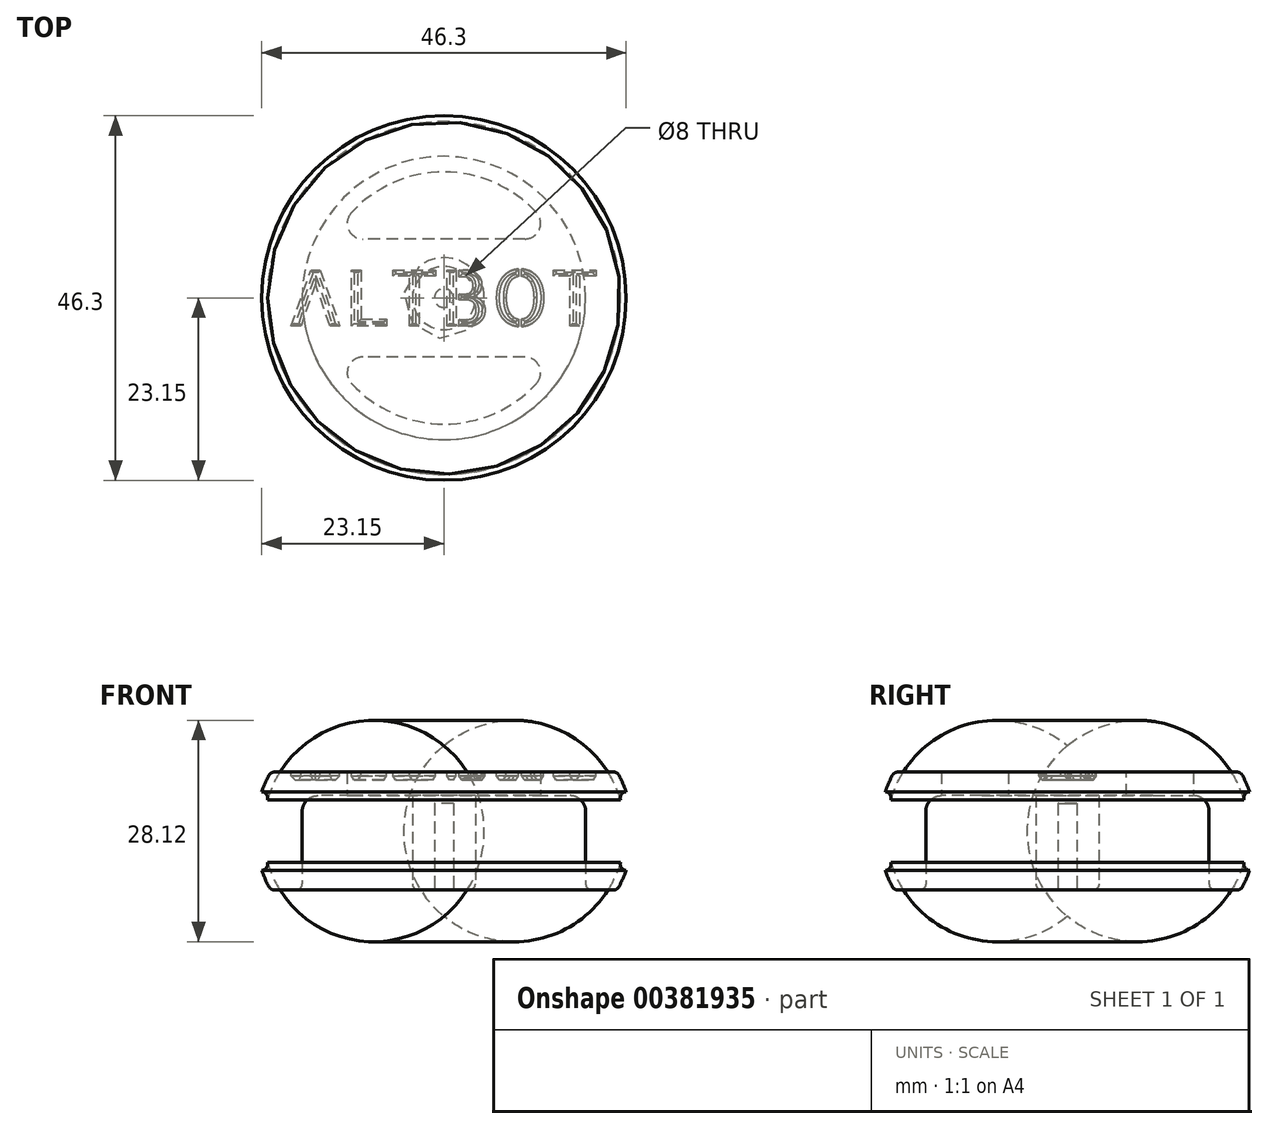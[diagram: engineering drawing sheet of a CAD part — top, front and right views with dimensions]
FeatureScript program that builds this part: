
annotation { "Feature Type Name" : "Feature", "Feature Type Description" : "" }
export const myFeature = defineFeature(function(context is Context, id is Id, definition is map)
    precondition{}
    {
        {
            assignVariable(context, id + "F0", {"name" : "EixoAltura", "anyValue" : 12});
        }
        {
            var Q0;
            Q0=qCreatedBy(makeId("Top.planeOp"),FACE);
            var sketch = newSketch(context, id + "F1", { "sketchPlane" : qUnion([Q0])});
            skCircle(sketch, "E0", {"center": v(0, 0) * mm, "radius": 4 * mm});
            skCircle(sketch, "E1", {"center": v(0, 0) * mm, "radius": 1.2 * mm});
            skSolve(sketch);
        }
        {
            var Q0;
            Q0=makeQuery(id+"F1.imprint","IMPRINT",FACE,{"disambiguationData":[TD([[makeQuery(id+"F1.imprint","IMPRINT",EDGE,{"derivedFrom":sQuery(id+"F1.wireOp",EDGE,"E1")}),1.0]])]});
            var Q1;
            Q1=makeQuery(id+"F1.imprint","IMPRINT",FACE,{"disambiguationData":[TD([[makeQuery(id+"F1.imprint","IMPRINT",EDGE,{"derivedFrom":sQuery(id+"F1.wireOp",EDGE,"E0")}),1.0]])]});
            extrude(context, id + "F2", {"entities" : qUnion([Q0, Q1]), "depth" : (getVariable(context, 'EixoAltura')) * mm});
        }
        {
            var Q0;
            Q0=makeQuery(id+"F1.imprint","IMPRINT",FACE,{"disambiguationData":[TD([[makeQuery(id+"F1.imprint","IMPRINT",EDGE,{"derivedFrom":sQuery(id+"F1.wireOp",EDGE,"E1")}),1.0]])]});
            var Q1;
            Q1 = qSketchRegion(id + "F4", true);
            extrude(context, id + "F3", {"entities" : qUnion([Q0, Q1]), "operationType" : NewBodyOperationType.REMOVE, "depth" : (getVariable(context, 'EixoAltura') - 1) * mm});
        }
        {
            var Q0;
            Q0=qCreatedBy(makeId("Right.planeOp"),FACE);
            var sketch = newSketch(context, id + "F4", { "sketchPlane" : qUnion([Q0])});
            skLineSegment(sketch, "E2", {"start": v(0, -22.32) * mm, "end": v(0, 36.65) * mm, "construction": true});
            skLineSegment(sketch, "E3", {"start": v(4, 12) * mm, "end": v(4, 0) * mm});
            skLineSegment(sketch, "E4", {"start": v(-4, 0) * mm, "end": v(-4, 12) * mm});
            skLineSegment(sketch, "E5", {"start": v(4, 12) * mm, "end": v(18, 12) * mm});
            skLineSegment(sketch, "E6", {"start": v(18, 12) * mm, "end": v(18, 0) * mm});
            skLineSegment(sketch, "E7", {"start": v(18, 0) * mm, "end": v(22, 0) * mm});
            skLineSegment(sketch, "E8", {"start": v(22, 0) * mm, "end": v(22, 15) * mm, "construction": true});
            skLineSegment(sketch, "E9", {"start": v(22, 15) * mm, "end": v(-22, 15) * mm});
            skLineSegment(sketch, "E10", {"start": v(-22, 15) * mm, "end": v(-22, 0) * mm, "construction": true});
            skLineSegment(sketch, "E11", {"start": v(-22, 0) * mm, "end": v(-18, 0) * mm});
            skLineSegment(sketch, "E12", {"start": v(-18, 0) * mm, "end": v(-18, 12) * mm});
            skLineSegment(sketch, "E13", {"start": v(-18, 12) * mm, "end": v(-4, 12) * mm});
            skLineSegment(sketch, "E14", {"start": v(22, 7.5) * mm, "end": v(24, 7.5) * mm, "construction": true});
            skPoint(sketch, "E14.endSnap0", {"position": v(22, 7.5) * mm});
            skLineSegment(sketch, "E15", {"start": v(-22, 7.5) * mm, "end": v(-24, 7.5) * mm, "construction": true});
            skPoint(sketch, "E15.endSnap0", {"position": v(-22, 7.5) * mm});
            skArc(sketch, "E16", {"start": v(22, 0) * mm, "mid": v(22.63, 1.22) * mm, "end": v(23.15, 2.5) * mm});
            skArc(sketch, "E17", {"start": v(-22, 15) * mm, "mid": v(-22.63, 13.78) * mm, "end": v(-23.15, 12.5) * mm});
            skArc(sketch, "E18.0", {"start": v(19.9, -1.3) * mm, "mid": v(21.14, 0.51) * mm, "end": v(22.08, 2.5) * mm, "construction": true});
            skArc(sketch, "E19.0", {"start": v(-19.83, 17.16) * mm, "mid": v(-21.44, 14.96) * mm, "end": v(-22.61, 12.5) * mm, "construction": true});
            skLineSegment(sketch, "E20.bottom", {"start": v(-19.5, 12.5) * mm, "end": v(-22.61, 12.5) * mm, "construction": true});
            skLineSegment(sketch, "E20.top", {"start": v(-19.5, 2.5) * mm, "end": v(-22.61, 2.5) * mm, "construction": true});
            skLineSegment(sketch, "E20.left", {"start": v(-19.5, 12.5) * mm, "end": v(-19.5, 2.5) * mm, "construction": true});
            skLineSegment(sketch, "E20.right", {"start": v(-24.5, 12.5) * mm, "end": v(-24.5, 2.5) * mm, "construction": true});
            skLineSegment(sketch, "E21.bottom", {"start": v(19.5, 12.5) * mm, "end": v(22.08, 12.5) * mm, "construction": true});
            skLineSegment(sketch, "E21.top", {"start": v(19.5, 2.5) * mm, "end": v(22.08, 2.5) * mm, "construction": true});
            skLineSegment(sketch, "E21.left", {"start": v(19.5, 12.5) * mm, "end": v(19.5, 2.5) * mm, "construction": true});
            skLineSegment(sketch, "E21.right", {"start": v(24.5, 12.5) * mm, "end": v(24.5, 2.5) * mm, "construction": true});
            skArc(sketch, "E22", {"start": v(-23.15, 12.5) * mm, "mid": v(-24, 7.5) * mm, "end": v(-23.15, 2.5) * mm, "construction": true});
            skLineSegment(sketch, "E23", {"start": v(-22.61, 12.5) * mm, "end": v(-23.15, 12.5) * mm});
            skArc(sketch, "E24", {"start": v(-22.61, 12.5) * mm, "mid": v(-23.5, 7.5) * mm, "end": v(-22.61, 2.5) * mm});
            skLineSegment(sketch, "E25", {"start": v(-23.15, 12.5) * mm, "end": v(-24.5, 12.5) * mm, "construction": true});
            skArc(sketch, "E26", {"start": v(-23.15, 2.5) * mm, "mid": v(-22.63, 1.22) * mm, "end": v(-22, 0) * mm});
            skLineSegment(sketch, "E27", {"start": v(-23.15, 2.5) * mm, "end": v(-24.5, 2.5) * mm, "construction": true});
            skLineSegment(sketch, "E28", {"start": v(-22.61, 2.5) * mm, "end": v(-23.15, 2.5) * mm});
            skLineSegment(sketch, "E29", {"start": v(-22.61, 2.5) * mm, "end": v(-22.61, 2.5) * mm});
            skLineSegment(sketch, "E30", {"start": v(23.15, 12.5) * mm, "end": v(24.5, 12.5) * mm, "construction": true});
            skArc(sketch, "E31", {"start": v(23.15, 12.5) * mm, "mid": v(22.63, 13.78) * mm, "end": v(22, 15) * mm});
            skArc(sketch, "E32", {"start": v(22.08, 12.5) * mm, "mid": v(21.14, 14.49) * mm, "end": v(19.9, 16.3) * mm, "construction": true});
            skLineSegment(sketch, "E33", {"start": v(22.08, 12.5) * mm, "end": v(23.15, 12.5) * mm});
            skArc(sketch, "E34", {"start": v(23.15, 2.5) * mm, "mid": v(24, 7.5) * mm, "end": v(23.15, 12.5) * mm, "construction": true});
            skLineSegment(sketch, "E35", {"start": v(23.15, 2.5) * mm, "end": v(24.5, 2.5) * mm, "construction": true});
            skArc(sketch, "E36", {"start": v(22.08, 2.5) * mm, "mid": v(23, 7.5) * mm, "end": v(22.08, 12.5) * mm});
            skLineSegment(sketch, "E37", {"start": v(22.08, 2.5) * mm, "end": v(23.15, 2.5) * mm});
            skArc(sketch, "E38", {"start": v(-22.61, 2.5) * mm, "mid": v(-21.44, 0.04) * mm, "end": v(-19.83, -2.16) * mm, "construction": true});
            skLineSegment(sketch, "E39", {"start": v(4, 12) * mm, "end": v(4, 12) * mm});
            skLineSegment(sketch, "E40", {"start": v(4, 12) * mm, "end": v(-4, 12) * mm});
            skLineSegment(sketch, "E41", {"start": v(0, 12) * mm, "end": v(0, 15) * mm});
            skSolve(sketch);
        }
        {
            var Q0;
            Q0=makeQuery(id+"F4.imprint","IMPRINT",FACE,{"disambiguationData":[TD([[makeQuery(id+"F4.imprint","IMPRINT",EDGE,{"derivedFrom":sQuery(id+"F4.wireOp",EDGE,"E5")}),1.0]])]});
            var Q1;
            Q1=sQuery(id+"F4.wireOp",EDGE,"E2");
            revolve(context, id + "F5", {"operationType" : NewBodyOperationType.ADD, "entities" : qUnion([Q0]), "axis" : qUnion([Q1]), "revolveType" : RevolveType.FULL});
        }
        {
            var Q0;
            Q0=makeQuery(id+"F5.opRevolve","SWEPT_FACE",FACE,{"disambiguationData":[OSD([sQuery(id+"F4.wireOp",EDGE,"E9")])]});
            var sketch = newSketch(context, id + "F6", { "sketchPlane" : qUnion([Q0])});
            skText(sketch, "E42", { "text": "ALTBOT", "fontName": "AllertaStencil-Regular.ttf"});
            const initialGuessF6  = {"E42": [-0.02, -0.00357, 1, 0, 0.00715]};
            skSetInitialGuess(sketch, initialGuessF6);
            skSolve(sketch);
        }
        {
            var Q0;
            Q0=makeQuery(id+"F6.imprint","IMPRINT",FACE,{"disambiguationData":[TD([[makeQuery(id+"F6.imprint","IMPRINT",EDGE,{"derivedFrom":sQuery(id+"F6.wireOp",EDGE,"E42.sketch_text.stroke-0")}),-1.0]])]});
            var Q1;
            Q1=makeQuery(id+"F6.imprint","IMPRINT",FACE,{"disambiguationData":[TD([[makeQuery(id+"F6.imprint","IMPRINT",EDGE,{"derivedFrom":sQuery(id+"F6.wireOp",EDGE,"E42.sketch_text.stroke-11")}),-1.0]])]});
            var Q2;
            Q2=makeQuery(id+"F6.imprint","IMPRINT",FACE,{"disambiguationData":[TD([[makeQuery(id+"F6.imprint","IMPRINT",EDGE,{"derivedFrom":sQuery(id+"F6.wireOp",EDGE,"E42.sketch_text.stroke-17")}),-1.0]])]});
            var Q3;
            Q3=makeQuery(id+"F6.imprint","IMPRINT",FACE,{"disambiguationData":[TD([[makeQuery(id+"F6.imprint","IMPRINT",EDGE,{"derivedFrom":sQuery(id+"F6.wireOp",EDGE,"E42.sketch_text.stroke-25")}),-1.0]])]});
            var Q4;
            Q4=makeQuery(id+"F6.imprint","IMPRINT",FACE,{"disambiguationData":[TD([[makeQuery(id+"F6.imprint","IMPRINT",EDGE,{"derivedFrom":sQuery(id+"F6.wireOp",EDGE,"E42.sketch_text.stroke-64")}),-1.0]])]});
            var Q5;
            Q5=makeQuery(id+"F6.imprint","IMPRINT",FACE,{"disambiguationData":[TD([[makeQuery(id+"F6.imprint","IMPRINT",EDGE,{"derivedFrom":sQuery(id+"F6.wireOp",EDGE,"E42.sketch_text.stroke-68")}),-1.0]])]});
            var Q6;
            Q6=makeQuery(id+"F6.imprint","IMPRINT",FACE,{"disambiguationData":[TD([[makeQuery(id+"F6.imprint","IMPRINT",EDGE,{"derivedFrom":sQuery(id+"F6.wireOp",EDGE,"E42.sketch_text.stroke-86")}),-1.0]])]});
            var Q7;
            Q7=makeQuery(id+"F6.imprint","IMPRINT",FACE,{"disambiguationData":[TD([[makeQuery(id+"F6.imprint","IMPRINT",EDGE,{"derivedFrom":sQuery(id+"F6.wireOp",EDGE,"E42.sketch_text.stroke-104")}),-1.0]])]});
            extrude(context, id + "F7", {"entities" : qUnion([Q0, Q1, Q2, Q3, Q4, Q5, Q6, Q7]), "operationType" : NewBodyOperationType.REMOVE, "oppositeDirection" : true, "depth" : .5 * mm});
        }
        {
            var Q0;
            Q0=makeQuery(id+"F7.boolean.opBoolean","COPY",FACE,{"derivedFrom":makeQuery(id+"F7.opExtrude","CAP_FACE",FACE,{"disambiguationData":[OSD([sQuery(id+"F6.wireOp",EDGE,"E42.sketch_text.stroke-0"),sQuery(id+"F6.wireOp",EDGE,"E42.sketch_text.stroke-1"),sQuery(id+"F6.wireOp",EDGE,"E42.sketch_text.stroke-2"),sQuery(id+"F6.wireOp",EDGE,"E42.sketch_text.stroke-3"),sQuery(id+"F6.wireOp",EDGE,"E42.sketch_text.stroke-4"),sQuery(id+"F6.wireOp",EDGE,"E42.sketch_text.stroke-5"),sQuery(id+"F6.wireOp",EDGE,"E42.sketch_text.stroke-6")])],"isStart":false})});
            var Q1;
            Q1=makeQuery(id+"F7.boolean.opBoolean","COPY",FACE,{"derivedFrom":makeQuery(id+"F7.opExtrude","CAP_FACE",FACE,{"disambiguationData":[OSD([sQuery(id+"F6.wireOp",EDGE,"E42.sketch_text.stroke-7"),sQuery(id+"F6.wireOp",EDGE,"E42.sketch_text.stroke-8"),sQuery(id+"F6.wireOp",EDGE,"E42.sketch_text.stroke-9"),sQuery(id+"F6.wireOp",EDGE,"E42.sketch_text.stroke-10")])],"isStart":false})});
            var Q2;
            Q2=makeQuery(id+"F7.boolean.opBoolean","COPY",FACE,{"derivedFrom":makeQuery(id+"F7.opExtrude","CAP_FACE",FACE,{"disambiguationData":[OSD([sQuery(id+"F6.wireOp",EDGE,"E42.sketch_text.stroke-11"),sQuery(id+"F6.wireOp",EDGE,"E42.sketch_text.stroke-12"),sQuery(id+"F6.wireOp",EDGE,"E42.sketch_text.stroke-13"),sQuery(id+"F6.wireOp",EDGE,"E42.sketch_text.stroke-14"),sQuery(id+"F6.wireOp",EDGE,"E42.sketch_text.stroke-15"),sQuery(id+"F6.wireOp",EDGE,"E42.sketch_text.stroke-16")])],"isStart":false})});
            var Q3;
            Q3=makeQuery(id+"F7.boolean.opBoolean","COPY",FACE,{"derivedFrom":makeQuery(id+"F7.opExtrude","CAP_FACE",FACE,{"disambiguationData":[OSD([sQuery(id+"F6.wireOp",EDGE,"E42.sketch_text.stroke-17"),sQuery(id+"F6.wireOp",EDGE,"E42.sketch_text.stroke-18"),sQuery(id+"F6.wireOp",EDGE,"E42.sketch_text.stroke-19"),sQuery(id+"F6.wireOp",EDGE,"E42.sketch_text.stroke-20"),sQuery(id+"F6.wireOp",EDGE,"E42.sketch_text.stroke-21"),sQuery(id+"F6.wireOp",EDGE,"E42.sketch_text.stroke-22"),sQuery(id+"F6.wireOp",EDGE,"E42.sketch_text.stroke-23"),sQuery(id+"F6.wireOp",EDGE,"E42.sketch_text.stroke-24")])],"isStart":false})});
            var Q4;
            Q4=makeQuery(id+"F7.boolean.opBoolean","COPY",FACE,{"derivedFrom":makeQuery(id+"F7.opExtrude","CAP_FACE",FACE,{"disambiguationData":[OSD([sQuery(id+"F6.wireOp",EDGE,"E42.sketch_text.stroke-64"),sQuery(id+"F6.wireOp",EDGE,"E42.sketch_text.stroke-65"),sQuery(id+"F6.wireOp",EDGE,"E42.sketch_text.stroke-66"),sQuery(id+"F6.wireOp",EDGE,"E42.sketch_text.stroke-67")])],"isStart":false})});
            var Q5;
            Q5=makeQuery(id+"F7.boolean.opBoolean","COPY",FACE,{"derivedFrom":makeQuery(id+"F7.opExtrude","CAP_FACE",FACE,{"disambiguationData":[OSD([sQuery(id+"F6.wireOp",EDGE,"E42.sketch_text.stroke-25"),sQuery(id+"F6.wireOp",EDGE,"E42.sketch_text.stroke-26"),sQuery(id+"F6.wireOp",EDGE,"E42.sketch_text.stroke-27"),sQuery(id+"F6.wireOp",EDGE,"E42.sketch_text.stroke-28"),sQuery(id+"F6.wireOp",EDGE,"E42.sketch_text.stroke-29"),sQuery(id+"F6.wireOp",EDGE,"E42.sketch_text.stroke-30"),sQuery(id+"F6.wireOp",EDGE,"E42.sketch_text.stroke-31"),sQuery(id+"F6.wireOp",EDGE,"E42.sketch_text.stroke-32"),sQuery(id+"F6.wireOp",EDGE,"E42.sketch_text.stroke-33"),sQuery(id+"F6.wireOp",EDGE,"E42.sketch_text.stroke-34"),sQuery(id+"F6.wireOp",EDGE,"E42.sketch_text.stroke-35"),sQuery(id+"F6.wireOp",EDGE,"E42.sketch_text.stroke-36"),sQuery(id+"F6.wireOp",EDGE,"E42.sketch_text.stroke-37"),sQuery(id+"F6.wireOp",EDGE,"E42.sketch_text.stroke-38"),sQuery(id+"F6.wireOp",EDGE,"E42.sketch_text.stroke-39"),sQuery(id+"F6.wireOp",EDGE,"E42.sketch_text.stroke-40"),sQuery(id+"F6.wireOp",EDGE,"E42.sketch_text.stroke-41"),sQuery(id+"F6.wireOp",EDGE,"E42.sketch_text.stroke-42"),sQuery(id+"F6.wireOp",EDGE,"E42.sketch_text.stroke-43"),sQuery(id+"F6.wireOp",EDGE,"E42.sketch_text.stroke-44"),sQuery(id+"F6.wireOp",EDGE,"E42.sketch_text.stroke-45"),sQuery(id+"F6.wireOp",EDGE,"E42.sketch_text.stroke-46"),sQuery(id+"F6.wireOp",EDGE,"E42.sketch_text.stroke-47"),sQuery(id+"F6.wireOp",EDGE,"E42.sketch_text.stroke-48"),sQuery(id+"F6.wireOp",EDGE,"E42.sketch_text.stroke-49"),sQuery(id+"F6.wireOp",EDGE,"E42.sketch_text.stroke-50"),sQuery(id+"F6.wireOp",EDGE,"E42.sketch_text.stroke-51"),sQuery(id+"F6.wireOp",EDGE,"E42.sketch_text.stroke-52"),sQuery(id+"F6.wireOp",EDGE,"E42.sketch_text.stroke-53"),sQuery(id+"F6.wireOp",EDGE,"E42.sketch_text.stroke-54"),sQuery(id+"F6.wireOp",EDGE,"E42.sketch_text.stroke-55"),sQuery(id+"F6.wireOp",EDGE,"E42.sketch_text.stroke-56"),sQuery(id+"F6.wireOp",EDGE,"E42.sketch_text.stroke-57"),sQuery(id+"F6.wireOp",EDGE,"E42.sketch_text.stroke-58"),sQuery(id+"F6.wireOp",EDGE,"E42.sketch_text.stroke-59"),sQuery(id+"F6.wireOp",EDGE,"E42.sketch_text.stroke-60"),sQuery(id+"F6.wireOp",EDGE,"E42.sketch_text.stroke-61"),sQuery(id+"F6.wireOp",EDGE,"E42.sketch_text.stroke-62"),sQuery(id+"F6.wireOp",EDGE,"E42.sketch_text.stroke-63")])],"isStart":false})});
            var Q6;
            Q6=makeQuery(id+"F7.boolean.opBoolean","COPY",FACE,{"derivedFrom":makeQuery(id+"F7.opExtrude","CAP_FACE",FACE,{"disambiguationData":[OSD([sQuery(id+"F6.wireOp",EDGE,"E42.sketch_text.stroke-68"),sQuery(id+"F6.wireOp",EDGE,"E42.sketch_text.stroke-69"),sQuery(id+"F6.wireOp",EDGE,"E42.sketch_text.stroke-70"),sQuery(id+"F6.wireOp",EDGE,"E42.sketch_text.stroke-71"),sQuery(id+"F6.wireOp",EDGE,"E42.sketch_text.stroke-72"),sQuery(id+"F6.wireOp",EDGE,"E42.sketch_text.stroke-73"),sQuery(id+"F6.wireOp",EDGE,"E42.sketch_text.stroke-74"),sQuery(id+"F6.wireOp",EDGE,"E42.sketch_text.stroke-75"),sQuery(id+"F6.wireOp",EDGE,"E42.sketch_text.stroke-76"),sQuery(id+"F6.wireOp",EDGE,"E42.sketch_text.stroke-77"),sQuery(id+"F6.wireOp",EDGE,"E42.sketch_text.stroke-78"),sQuery(id+"F6.wireOp",EDGE,"E42.sketch_text.stroke-79"),sQuery(id+"F6.wireOp",EDGE,"E42.sketch_text.stroke-80"),sQuery(id+"F6.wireOp",EDGE,"E42.sketch_text.stroke-81"),sQuery(id+"F6.wireOp",EDGE,"E42.sketch_text.stroke-82"),sQuery(id+"F6.wireOp",EDGE,"E42.sketch_text.stroke-83"),sQuery(id+"F6.wireOp",EDGE,"E42.sketch_text.stroke-84"),sQuery(id+"F6.wireOp",EDGE,"E42.sketch_text.stroke-85")])],"isStart":false})});
            var Q7;
            Q7=makeQuery(id+"F7.boolean.opBoolean","COPY",FACE,{"derivedFrom":makeQuery(id+"F7.opExtrude","CAP_FACE",FACE,{"disambiguationData":[OSD([sQuery(id+"F6.wireOp",EDGE,"E42.sketch_text.stroke-86"),sQuery(id+"F6.wireOp",EDGE,"E42.sketch_text.stroke-87"),sQuery(id+"F6.wireOp",EDGE,"E42.sketch_text.stroke-88"),sQuery(id+"F6.wireOp",EDGE,"E42.sketch_text.stroke-89"),sQuery(id+"F6.wireOp",EDGE,"E42.sketch_text.stroke-90"),sQuery(id+"F6.wireOp",EDGE,"E42.sketch_text.stroke-91"),sQuery(id+"F6.wireOp",EDGE,"E42.sketch_text.stroke-92"),sQuery(id+"F6.wireOp",EDGE,"E42.sketch_text.stroke-93"),sQuery(id+"F6.wireOp",EDGE,"E42.sketch_text.stroke-94"),sQuery(id+"F6.wireOp",EDGE,"E42.sketch_text.stroke-95"),sQuery(id+"F6.wireOp",EDGE,"E42.sketch_text.stroke-96"),sQuery(id+"F6.wireOp",EDGE,"E42.sketch_text.stroke-97"),sQuery(id+"F6.wireOp",EDGE,"E42.sketch_text.stroke-98"),sQuery(id+"F6.wireOp",EDGE,"E42.sketch_text.stroke-99"),sQuery(id+"F6.wireOp",EDGE,"E42.sketch_text.stroke-100"),sQuery(id+"F6.wireOp",EDGE,"E42.sketch_text.stroke-101"),sQuery(id+"F6.wireOp",EDGE,"E42.sketch_text.stroke-102"),sQuery(id+"F6.wireOp",EDGE,"E42.sketch_text.stroke-103")])],"isStart":false})});
            var Q8;
            Q8=makeQuery(id+"F7.boolean.opBoolean","COPY",FACE,{"derivedFrom":makeQuery(id+"F7.opExtrude","CAP_FACE",FACE,{"disambiguationData":[OSD([sQuery(id+"F6.wireOp",EDGE,"E42.sketch_text.stroke-104"),sQuery(id+"F6.wireOp",EDGE,"E42.sketch_text.stroke-105"),sQuery(id+"F6.wireOp",EDGE,"E42.sketch_text.stroke-106"),sQuery(id+"F6.wireOp",EDGE,"E42.sketch_text.stroke-107"),sQuery(id+"F6.wireOp",EDGE,"E42.sketch_text.stroke-108"),sQuery(id+"F6.wireOp",EDGE,"E42.sketch_text.stroke-109"),sQuery(id+"F6.wireOp",EDGE,"E42.sketch_text.stroke-110"),sQuery(id+"F6.wireOp",EDGE,"E42.sketch_text.stroke-111")])],"isStart":false})});
            extrude(context, id + "F8", {"entities" : qUnion([Q0, Q1, Q2, Q3, Q4, Q5, Q6, Q7, Q8]), "operationType" : NewBodyOperationType.REMOVE, "oppositeDirection" : true, "depth" : .5 * mm, "hasDraft" : true, "draftAngle" : 35 * degree, "draftPullDirection" : true});
        }
        {
            var Q0;
            Q0=makeQuery(id+"F5.opRevolve","SWEPT_EDGE",EDGE,{"disambiguationData":[OSD([sQuery(id+"F4.wireOp",EDGE,"E33"),sQuery(id+"F4.wireOp",EDGE,"E36")])]});
            var Q1;
            Q1=makeQuery(id+"F5.opRevolve","SWEPT_EDGE",EDGE,{"disambiguationData":[OSD([sQuery(id+"F4.wireOp",EDGE,"E36"),sQuery(id+"F4.wireOp",EDGE,"E37")])]});
            var Q2;
            Q2=makeQuery(id+"F5.opRevolve","SWEPT_EDGE",EDGE,{"disambiguationData":[OSD([sQuery(id+"F4.wireOp",EDGE,"E9"),sQuery(id+"F4.wireOp",EDGE,"E31")])]});
            var Q3;
            Q3=makeQuery(id+"F5.opRevolve","SWEPT_EDGE",EDGE,{"disambiguationData":[OSD([sQuery(id+"F4.wireOp",EDGE,"E7"),sQuery(id+"F4.wireOp",EDGE,"E16")])]});
            var Q4;
            Q4=makeQuery(id+"F5.opRevolve","SWEPT_EDGE",EDGE,{"disambiguationData":[OSD([sQuery(id+"F4.wireOp",EDGE,"E6"),sQuery(id+"F4.wireOp",EDGE,"E7")])]});
            var Q5;
            Q5=makeQuery(id+"F3.boolean.opBoolean","COPY",EDGE,{"derivedFrom":makeQuery(id+"F3.opExtrude","CAP_EDGE",EDGE,{"disambiguationData":[OSD([sQuery(id+"F1.wireOp",EDGE,"E1")])],"isStart":true})});
            var Q6;
            Q6=makeQuery(id+"F2.opExtrude","CAP_EDGE",EDGE,{"disambiguationData":[OSD([sQuery(id+"F1.wireOp",EDGE,"E0")])],"isStart":true});
            fillet(context, id + "F9", {"entities" : qUnion([Q0, Q1, Q2, Q3, Q4, Q5, Q6]), "radius" : .8 * mm, "tangentPropagation" : true, "allowEdgeOverflow" : false});
        }
        {
            var Q0;
            Q0=makeQuery(id+"F5.boolean.opBoolean","MERGE",EDGE,{"derivedFrom":[makeQuery(id+"F2.opExtrude","CAP_EDGE",EDGE,{"disambiguationData":[OSD([sQuery(id+"F1.wireOp",EDGE,"E0")])],"isStart":false}),makeQuery(id+"F5.opRevolve","SWEPT_EDGE",EDGE,{"disambiguationData":[OSD([sQuery(id+"F4.wireOp",EDGE,"E5"),sQuery(id+"F4.wireOp",EDGE,"E39")])]})]});
            var Q1;
            Q1=makeQuery(id+"F5.opRevolve","SWEPT_EDGE",EDGE,{"disambiguationData":[OSD([sQuery(id+"F4.wireOp",EDGE,"E5"),sQuery(id+"F4.wireOp",EDGE,"E6")])]});
            fillet(context, id + "F10", {"entities" : qUnion([Q0, Q1]), "radius" : 2 * mm, "tangentPropagation" : true, "allowEdgeOverflow" : false});
        }
        {
            var Q0;
            Q0=makeQuery(id+"F5.opRevolve","SWEPT_FACE",FACE,{"disambiguationData":[OSD([sQuery(id+"F4.wireOp",EDGE,"E5")])]});
            var sketch = newSketch(context, id + "F11", { "sketchPlane" : qUnion([Q0])});
            skLineSegment(sketch, "E43.bottom", {"start": v(26.08, 7.5) * mm, "end": v(-26.08, 7.5) * mm});
            skLineSegment(sketch, "E43.top", {"start": v(26.08, -7.5) * mm, "end": v(-26.08, -7.5) * mm});
            skLineSegment(sketch, "E43.left", {"start": v(26.08, 7.5) * mm, "end": v(26.08, -7.5) * mm});
            skLineSegment(sketch, "E43.right", {"start": v(-26.08, 7.5) * mm, "end": v(-26.08, -7.5) * mm});
            skPoint(sketch, "E43.middle", {"position": v(0, 0) * mm});
            skSolve(sketch);
        }
        {
            var Q0;
            {var subQ0=sQuery(id+"F11.wireOp",EDGE,"E43.bottom");var subQ1=sQuery(id+"F4.wireOp",EDGE,"E5");var subQ2=makeQuery(id+"F10.opFillet","BLEND_EDGE",EDGE,{"blendedFrom":[makeQuery(id+"F5.opRevolve","SWEPT_EDGE",EDGE,{"disambiguationData":[OSD([subQ1,sQuery(id+"F4.wireOp",EDGE,"E6")])]}),makeQuery(id+"F5.opRevolve","SWEPT_FACE",FACE,{"disambiguationData":[OSD([subQ1])]})],"blendedInto":[makeQuery(id+"F5.opRevolve","SWEPT_FACE",FACE,{"disambiguationData":[OSD([subQ1])]})]});var subQ3=makeQuery(id+"F11.imprint","INTERSECT",VERTEX,{"disambiguationData":[OD(0.0)],"derivedFrom":[subQ2,subQ0]});Q0=makeQuery(id+"F11.imprint","IMPRINT",FACE,{"disambiguationData":[TD([[makeQuery(id+"F11.imprint","IMPRINT",EDGE,{"disambiguationData":[TD([[subQ3,-1.0]])],"derivedFrom":subQ0}),-1.0]])]});}
            var Q1;
            {var subQ0=sQuery(id+"F11.wireOp",EDGE,"E43.top");var subQ1=sQuery(id+"F4.wireOp",EDGE,"E5");var subQ2=makeQuery(id+"F10.opFillet","BLEND_EDGE",EDGE,{"blendedFrom":[makeQuery(id+"F5.opRevolve","SWEPT_EDGE",EDGE,{"disambiguationData":[OSD([subQ1,sQuery(id+"F4.wireOp",EDGE,"E6")])]}),makeQuery(id+"F5.opRevolve","SWEPT_FACE",FACE,{"disambiguationData":[OSD([subQ1])]})],"blendedInto":[makeQuery(id+"F5.opRevolve","SWEPT_FACE",FACE,{"disambiguationData":[OSD([subQ1])]})]});var subQ3=makeQuery(id+"F11.imprint","INTERSECT",VERTEX,{"disambiguationData":[OD(0.0)],"derivedFrom":[subQ2,subQ0]});Q1=makeQuery(id+"F11.imprint","IMPRINT",FACE,{"disambiguationData":[TD([[makeQuery(id+"F11.imprint","IMPRINT",EDGE,{"disambiguationData":[TD([[subQ3,-1.0]])],"derivedFrom":subQ0}),1.0]])]});}
            extrude(context, id + "F12", {"entities" : qUnion([Q0, Q1]), "operationType" : NewBodyOperationType.REMOVE, "endBound" : BoundingType.UP_TO_NEXT, "oppositeDirection" : true, "depth" : 25 * mm});
        }
        {
            var Q0;
            {var subQ0=sQuery(id+"F11.wireOp",EDGE,"E43.top");var subQ1=sQuery(id+"F4.wireOp",EDGE,"E5");var subQ2=sQuery(id+"F4.wireOp",EDGE,"E6");Q0=makeQuery(id+"F12.boolean.opBoolean","COPY",EDGE,{"derivedFrom":makeQuery(id+"F12.opExtrude","SWEPT_EDGE",EDGE,{"disambiguationData":[OSD([subQ1,subQ2,subQ0]),TDD([makeQuery(id+"F11.imprint","INTERSECT",VERTEX,{"disambiguationData":[OD(0.0)],"derivedFrom":[makeQuery(id+"F10.opFillet","BLEND_EDGE",EDGE,{"blendedFrom":[makeQuery(id+"F5.opRevolve","SWEPT_EDGE",EDGE,{"disambiguationData":[OSD([subQ1,subQ2])]}),makeQuery(id+"F5.opRevolve","SWEPT_FACE",FACE,{"disambiguationData":[OSD([subQ1])]})],"blendedInto":[makeQuery(id+"F5.opRevolve","SWEPT_FACE",FACE,{"disambiguationData":[OSD([subQ1])]})]}),subQ0]})])]})});}
            var Q1;
            {var subQ0=sQuery(id+"F11.wireOp",EDGE,"E43.top");var subQ1=sQuery(id+"F4.wireOp",EDGE,"E5");var subQ2=sQuery(id+"F4.wireOp",EDGE,"E6");Q1=makeQuery(id+"F12.boolean.opBoolean","COPY",EDGE,{"derivedFrom":makeQuery(id+"F12.opExtrude","SWEPT_EDGE",EDGE,{"disambiguationData":[OSD([subQ1,subQ2,subQ0]),TDD([makeQuery(id+"F11.imprint","INTERSECT",VERTEX,{"disambiguationData":[OD(1.0)],"derivedFrom":[makeQuery(id+"F10.opFillet","BLEND_EDGE",EDGE,{"blendedFrom":[makeQuery(id+"F5.opRevolve","SWEPT_EDGE",EDGE,{"disambiguationData":[OSD([subQ1,subQ2])]}),makeQuery(id+"F5.opRevolve","SWEPT_FACE",FACE,{"disambiguationData":[OSD([subQ1])]})],"blendedInto":[makeQuery(id+"F5.opRevolve","SWEPT_FACE",FACE,{"disambiguationData":[OSD([subQ1])]})]}),subQ0]})])]})});}
            var Q2;
            {var subQ0=sQuery(id+"F11.wireOp",EDGE,"E43.bottom");var subQ1=sQuery(id+"F4.wireOp",EDGE,"E5");var subQ2=sQuery(id+"F4.wireOp",EDGE,"E6");Q2=makeQuery(id+"F12.boolean.opBoolean","COPY",EDGE,{"derivedFrom":makeQuery(id+"F12.opExtrude","SWEPT_EDGE",EDGE,{"disambiguationData":[OSD([subQ1,subQ2,subQ0]),TDD([makeQuery(id+"F11.imprint","INTERSECT",VERTEX,{"disambiguationData":[OD(1.0)],"derivedFrom":[makeQuery(id+"F10.opFillet","BLEND_EDGE",EDGE,{"blendedFrom":[makeQuery(id+"F5.opRevolve","SWEPT_EDGE",EDGE,{"disambiguationData":[OSD([subQ1,subQ2])]}),makeQuery(id+"F5.opRevolve","SWEPT_FACE",FACE,{"disambiguationData":[OSD([subQ1])]})],"blendedInto":[makeQuery(id+"F5.opRevolve","SWEPT_FACE",FACE,{"disambiguationData":[OSD([subQ1])]})]}),subQ0]})])]})});}
            var Q3;
            {var subQ0=sQuery(id+"F11.wireOp",EDGE,"E43.bottom");var subQ1=sQuery(id+"F4.wireOp",EDGE,"E5");var subQ2=sQuery(id+"F4.wireOp",EDGE,"E6");Q3=makeQuery(id+"F12.boolean.opBoolean","COPY",EDGE,{"derivedFrom":makeQuery(id+"F12.opExtrude","SWEPT_EDGE",EDGE,{"disambiguationData":[OSD([subQ1,subQ2,subQ0]),TDD([makeQuery(id+"F11.imprint","INTERSECT",VERTEX,{"disambiguationData":[OD(0.0)],"derivedFrom":[makeQuery(id+"F10.opFillet","BLEND_EDGE",EDGE,{"blendedFrom":[makeQuery(id+"F5.opRevolve","SWEPT_EDGE",EDGE,{"disambiguationData":[OSD([subQ1,subQ2])]}),makeQuery(id+"F5.opRevolve","SWEPT_FACE",FACE,{"disambiguationData":[OSD([subQ1])]})],"blendedInto":[makeQuery(id+"F5.opRevolve","SWEPT_FACE",FACE,{"disambiguationData":[OSD([subQ1])]})]}),subQ0]})])]})});}
            var Q4;
            {var subQ0=sQuery(id+"F11.wireOp",EDGE,"E43.bottom");var subQ1=sQuery(id+"F4.wireOp",EDGE,"E5");var subQ2=makeQuery(id+"F10.opFillet","BLEND_EDGE",EDGE,{"blendedFrom":[makeQuery(id+"F5.opRevolve","SWEPT_EDGE",EDGE,{"disambiguationData":[OSD([subQ1,sQuery(id+"F4.wireOp",EDGE,"E6")])]}),makeQuery(id+"F5.opRevolve","SWEPT_FACE",FACE,{"disambiguationData":[OSD([subQ1])]})],"blendedInto":[makeQuery(id+"F5.opRevolve","SWEPT_FACE",FACE,{"disambiguationData":[OSD([subQ1])]})]});Q4=makeQuery(id+"F12.boolean.opBoolean","COPY",EDGE,{"derivedFrom":makeQuery(id+"F12.opExtrude","TWEAK_EDGE",EDGE,{"derivedFrom":[makeQuery(id+"F5.opRevolve","SWEPT_FACE",FACE,{"disambiguationData":[OSD([sQuery(id+"F4.wireOp",EDGE,"E9")])]}),makeQuery(id+"F11.imprint","IMPRINT",EDGE,{"disambiguationData":[TD([[makeQuery(id+"F11.imprint","INTERSECT",VERTEX,{"disambiguationData":[OD(0.0)],"derivedFrom":[subQ2,subQ0]}),-1.0]])],"derivedFrom":subQ2})]})});}
            var Q5;
            {var subQ0=sQuery(id+"F11.wireOp",EDGE,"E43.bottom");var subQ1=sQuery(id+"F4.wireOp",EDGE,"E5");var subQ2=makeQuery(id+"F10.opFillet","BLEND_EDGE",EDGE,{"blendedFrom":[makeQuery(id+"F5.opRevolve","SWEPT_EDGE",EDGE,{"disambiguationData":[OSD([subQ1,sQuery(id+"F4.wireOp",EDGE,"E6")])]}),makeQuery(id+"F5.opRevolve","SWEPT_FACE",FACE,{"disambiguationData":[OSD([subQ1])]})],"blendedInto":[makeQuery(id+"F5.opRevolve","SWEPT_FACE",FACE,{"disambiguationData":[OSD([subQ1])]})]});Q5=makeQuery(id+"F12.boolean.opBoolean","COPY",EDGE,{"derivedFrom":makeQuery(id+"F12.opExtrude","TWEAK_EDGE",EDGE,{"derivedFrom":[makeQuery(id+"F5.opRevolve","SWEPT_FACE",FACE,{"disambiguationData":[OSD([sQuery(id+"F4.wireOp",EDGE,"E9")])]}),makeQuery(id+"F11.imprint","IMPRINT",EDGE,{"disambiguationData":[TD([[makeQuery(id+"F11.imprint","INTERSECT",VERTEX,{"disambiguationData":[OD(0.0)],"derivedFrom":[subQ2,subQ0]}),-1.0]])],"derivedFrom":subQ0})]})});}
            var Q6;
            {var subQ0=sQuery(id+"F11.wireOp",EDGE,"E43.top");var subQ1=sQuery(id+"F4.wireOp",EDGE,"E5");var subQ2=makeQuery(id+"F10.opFillet","BLEND_EDGE",EDGE,{"blendedFrom":[makeQuery(id+"F5.opRevolve","SWEPT_EDGE",EDGE,{"disambiguationData":[OSD([subQ1,sQuery(id+"F4.wireOp",EDGE,"E6")])]}),makeQuery(id+"F5.opRevolve","SWEPT_FACE",FACE,{"disambiguationData":[OSD([subQ1])]})],"blendedInto":[makeQuery(id+"F5.opRevolve","SWEPT_FACE",FACE,{"disambiguationData":[OSD([subQ1])]})]});Q6=makeQuery(id+"F12.boolean.opBoolean","COPY",EDGE,{"derivedFrom":makeQuery(id+"F12.opExtrude","TWEAK_EDGE",EDGE,{"derivedFrom":[makeQuery(id+"F5.opRevolve","SWEPT_FACE",FACE,{"disambiguationData":[OSD([sQuery(id+"F4.wireOp",EDGE,"E9")])]}),makeQuery(id+"F11.imprint","IMPRINT",EDGE,{"disambiguationData":[TD([[makeQuery(id+"F11.imprint","INTERSECT",VERTEX,{"disambiguationData":[OD(0.0)],"derivedFrom":[subQ2,subQ0]}),-1.0]])],"derivedFrom":subQ0})]})});}
            var Q7;
            {var subQ0=sQuery(id+"F11.wireOp",EDGE,"E43.top");var subQ1=sQuery(id+"F4.wireOp",EDGE,"E5");var subQ2=makeQuery(id+"F10.opFillet","BLEND_EDGE",EDGE,{"blendedFrom":[makeQuery(id+"F5.opRevolve","SWEPT_EDGE",EDGE,{"disambiguationData":[OSD([subQ1,sQuery(id+"F4.wireOp",EDGE,"E6")])]}),makeQuery(id+"F5.opRevolve","SWEPT_FACE",FACE,{"disambiguationData":[OSD([subQ1])]})],"blendedInto":[makeQuery(id+"F5.opRevolve","SWEPT_FACE",FACE,{"disambiguationData":[OSD([subQ1])]})]});Q7=makeQuery(id+"F12.boolean.opBoolean","COPY",EDGE,{"derivedFrom":makeQuery(id+"F12.opExtrude","TWEAK_EDGE",EDGE,{"derivedFrom":[makeQuery(id+"F5.opRevolve","SWEPT_FACE",FACE,{"disambiguationData":[OSD([sQuery(id+"F4.wireOp",EDGE,"E9")])]}),makeQuery(id+"F11.imprint","IMPRINT",EDGE,{"disambiguationData":[TD([[makeQuery(id+"F11.imprint","INTERSECT",VERTEX,{"disambiguationData":[OD(0.0)],"derivedFrom":[subQ2,subQ0]}),1.0]])],"derivedFrom":subQ2})]})});}
            fillet(context, id + "F13", {"entities" : qUnion([Q0, Q1, Q2, Q3, Q4, Q5, Q6, Q7]), "radius" : 2 * mm, "tangentPropagation" : true, "allowEdgeOverflow" : false});
        }
    });
